# Revit family: Animo L-Shaped Handrail_
name_source: partatom
category: Casework
revit_build: Autodesk Revit Architecture 2012 (Build: 20110916_2132(x64)
units: mm (PartAtom-declared; Revit-internal decimal feet)

## types (12) — shared parameters
Installation Height = 850 mm  [stored 2.78871 ft]

## per-type parameters (varying)
| type | Handrail Color | Height | Width |
| 1624 | RAL 9010 - White | 440 mm  [stored 1.44357 ft] | 590 mm  [stored 1.9357 ft] |
| 1624 P | RAL 3003 - Red | 440 mm  [stored 1.44357 ft] | 590 mm  [stored 1.9357 ft] |
| 1624 K | RAL 1004 - Yellow | 440 mm  [stored 1.44357 ft] | 590 mm  [stored 1.9357 ft] |
| 1624 H | RAL 7037 - Grey | 440 mm  [stored 1.44357 ft] | 590 mm  [stored 1.9357 ft] |
| 1628 | RAL 9010 - White | 440 mm  [stored 1.44357 ft] | 990 mm  [stored 3.24803 ft] |
| 1628 H | RAL 7037 - Grey | 440 mm  [stored 1.44357 ft] | 990 mm  [stored 3.24803 ft] |
| 1628 K | RAL 1004 - Yellow | 440 mm  [stored 1.44357 ft] | 990 mm  [stored 3.24803 ft] |
| 1628 P | RAL 3003 - Red | 440 mm  [stored 1.44357 ft] | 990 mm  [stored 3.24803 ft] |
| 1636 | RAL 9010 - White | 790 mm  [stored 2.59186 ft] | 590 mm  [stored 1.9357 ft] |
| 1636 H | RAL 7037 - Grey | 790 mm  [stored 2.59186 ft] | 590 mm  [stored 1.9357 ft] |
| 1636 P | RAL 3003 - Red | 790 mm  [stored 2.59186 ft] | 590 mm  [stored 1.9357 ft] |
| 1636 K | RAL 1004 - Yellow | 790 mm  [stored 2.59186 ft] | 590 mm  [stored 1.9357 ft] |

note: [stored X ft] marks values corroborated as IEEE doubles in the binary element streams (Revit-internal decimal feet)

## geometry (parser evidence)
native form markers: Sweep x4
no freeform markers — native parametric forms only
